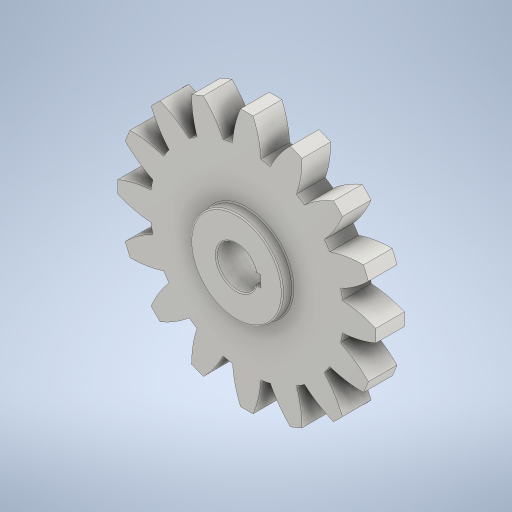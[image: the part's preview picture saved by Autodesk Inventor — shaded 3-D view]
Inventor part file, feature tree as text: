
AUTODESK INVENTOR PART (.ipt)
format: ipt  version: 2024.2 (Build 282272000, 272)  size: 460,288 bytes
history: native  units: mm (DEFAULTED — no unit token found)
features: extrude x4, sketch x4, plane x3, other x3, fillet x1, projected_geometry x1
ambient origin geometry x8: Origin, YZ Plane, XZ Plane, XY Plane, X Axis, Y Axis, Z Axis, Center Point
bodies: Solid1 (feature_tree)
feature tree (16):
  extrude  "Extrusion1"  Depth=25.0mm TaperAngle=0.0deg
  plane  "Work Plane2"
  plane  "Work Plane8"
  plane  "Work Plane9"
  other  "Spur Gear"
  extrude  "Extrusion2"  Depth=10.0mm TaperAngle=0.0deg
  extrude  "Extrusion3"  Depth=1.963495mm TaperAngle=0.0deg
  extrude  "Extrusion4"  TaperAngle=0.0deg  [1 undecoded]
  fillet  "Fillet1"  Radius=494.0mm
  sketch  "Sketch1"  dims[d0=225.11376mm d1=25.0mm d2=0.0mm]
  other  "Srf1"
  sketch  "Sketch3"  dims[d3=200.10112mm d4=10.0mm d5=0.0mm]
  projected_geometry  "Projected Loop1"
  sketch  "Sketch5"  dims[d16=494.0mm d17=0.0mm d34=1.963495mm]
  sketch  "Sketch6"  dims[d39=0.0mm d41=0.0mm d43=494.0mm d46=494.0mm d47=0.0mm d48=0.0mm d51=35.0mm d52=0.0mm d53=0.0mm d55=80.0mm d56=35.0mm d57=9.0mm d58=0.0mm d59=21.0mm d60=10.0mm d61=0.0mm d62=0.0mm d63=1.0mm]
  other  "Pitch Diameter"
note: 1 required parameter value undecoded (feature->parameter linkage not recoverable at this tier; creation-order binding heuristic only, values carry confidence <= 0.55)
